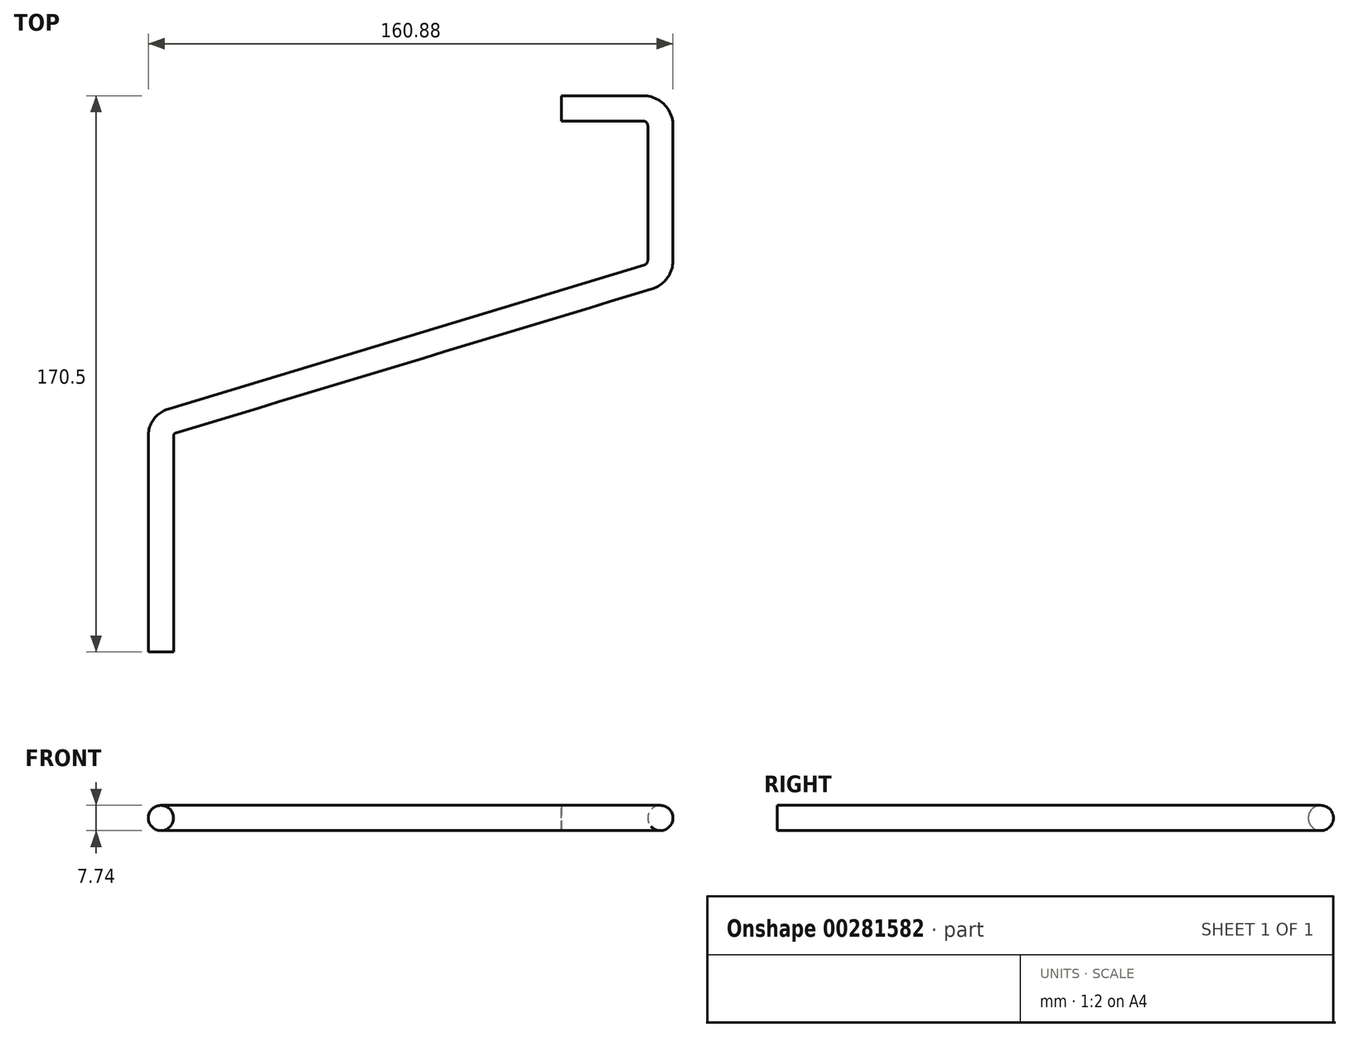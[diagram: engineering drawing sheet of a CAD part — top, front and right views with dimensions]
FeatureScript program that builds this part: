
annotation { "Feature Type Name" : "Feature", "Feature Type Description" : "" }
export const myFeature = defineFeature(function(context is Context, id is Id, definition is map)
    precondition{}
    {
        {
            var Q0;
            Q0=qCreatedBy(makeId("Top.planeOp"),FACE);
            var sketch = newSketch(context, id + "F0", { "sketchPlane" : qUnion([Q0])});
            skLineSegment(sketch, "E0", {"start": v(0, 0) * mm, "end": v(25, 0) * mm});
            skLineSegment(sketch, "E1", {"start": v(30, -5) * mm, "end": v(30, -46.29) * mm});
            skLineSegment(sketch, "E2", {"start": v(26.45, -51.07) * mm, "end": v(-119.6, -95.26) * mm});
            skLineSegment(sketch, "E3", {"start": v(-123.14, -100.05) * mm, "end": v(-123.14, -166.34) * mm});
            skPoint(sketch, "E4.visualSharp", {"position": v(-123.14, -96.34) * mm});
            skArc(sketch, "E4.filletArc", {"start": v(-119.6, -95.26) * mm, "mid": v(-122.16, -97.07) * mm, "end": v(-123.14, -100.05) * mm});
            skPoint(sketch, "E5.visualSharp", {"position": v(30, -50) * mm});
            skArc(sketch, "E5.filletArc", {"start": v(26.45, -51.07) * mm, "mid": v(29.01, -49.27) * mm, "end": v(30, -46.29) * mm});
            skPoint(sketch, "E6.visualSharp", {"position": v(30, 0) * mm});
            skArc(sketch, "E6.filletArc", {"start": v(30, -5) * mm, "mid": v(28.54, -1.46) * mm, "end": v(25, 0) * mm});
            skSolve(sketch);
        }
        {
            var Q0;
            Q0=sQuery(id+"F0.wireOp",VERTEX,"E3.end");
            var Q1;
            Q1=sQuery(id+"F0.wireOp",EDGE,"E3");
            cPlane(context, id + "F1", {"entities" : qUnion([Q0, Q1]), "cplaneType" : CPlaneType.LINE_POINT, "offset" : 25 * mm, "width" : 150 * mm, "height" : 150 * mm});
        }
        {
            var Q0;
            Q0=qCreatedBy(id+"F1.planeOp",FACE);
            var sketch = newSketch(context, id + "F2", { "sketchPlane" : qUnion([Q0])});
            skCircle(sketch, "E7", {"center": v(-122.85, 0) * mm, "radius": 3.87 * mm});
            skSolve(sketch);
        }
        {
            var Q0;
            Q0=makeQuery(id+"F2.imprint","IMPRINT",FACE,{"disambiguationData":[TD([[makeQuery(id+"F2.imprint","IMPRINT",EDGE,{"derivedFrom":sQuery(id+"F2.wireOp",EDGE,"E7")}),1.0]])]});
            var Q1;
            Q1 = qConstructionFilter(qBodyType(qCreatedBy(id + "F0" ,EDGE), BodyType.WIRE), ConstructionObject.NO);
            sweep(context, id + "F3", {"profiles" : qUnion([Q0]), "path" : qUnion([Q1])});
        }
    });
